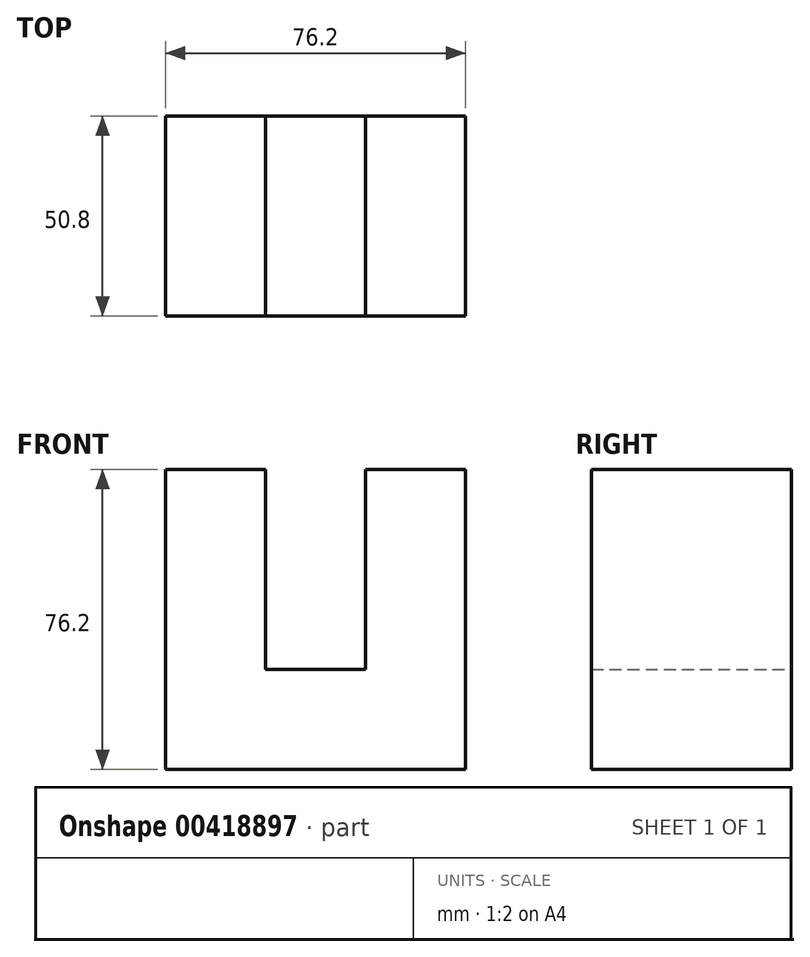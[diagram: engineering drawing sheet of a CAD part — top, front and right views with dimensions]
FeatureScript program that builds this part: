
annotation { "Feature Type Name" : "Feature", "Feature Type Description" : "" }
export const myFeature = defineFeature(function(context is Context, id is Id, definition is map)
    precondition{}
    {
        {
            var Q0;
            Q0=qCreatedBy(makeId("Front.planeOp"),FACE);
            var sketch = newSketch(context, id + "F0", { "sketchPlane" : qUnion([Q0])});
            skLineSegment(sketch, "E0", {"start": v(0, 0) * mm, "end": v(-76.2, 0) * mm});
            skLineSegment(sketch, "E1", {"start": v(-76.2, 0) * mm, "end": v(-76.2, 76.2) * mm});
            skLineSegment(sketch, "E2", {"start": v(-76.2, 76.2) * mm, "end": v(-50.8, 76.2) * mm});
            skLineSegment(sketch, "E3", {"start": v(-50.8, 76.2) * mm, "end": v(-50.8, 25.4) * mm});
            skLineSegment(sketch, "E4", {"start": v(-50.8, 25.4) * mm, "end": v(-25.4, 25.4) * mm});
            skLineSegment(sketch, "E5", {"start": v(-25.4, 25.4) * mm, "end": v(-25.4, 76.2) * mm});
            skLineSegment(sketch, "E6", {"start": v(-25.4, 76.2) * mm, "end": v(0, 76.2) * mm});
            skLineSegment(sketch, "E7", {"start": v(0, 76.2) * mm, "end": v(0, -3.06) * mm});
            skSolve(sketch);
        }
        {
            var Q0;
            Q0 = qSketchRegion(id + "F0", true);
            extrude(context, id + "F1", {"entities" : qUnion([Q0]), "depth" : 50.8 * mm});
        }
    });
